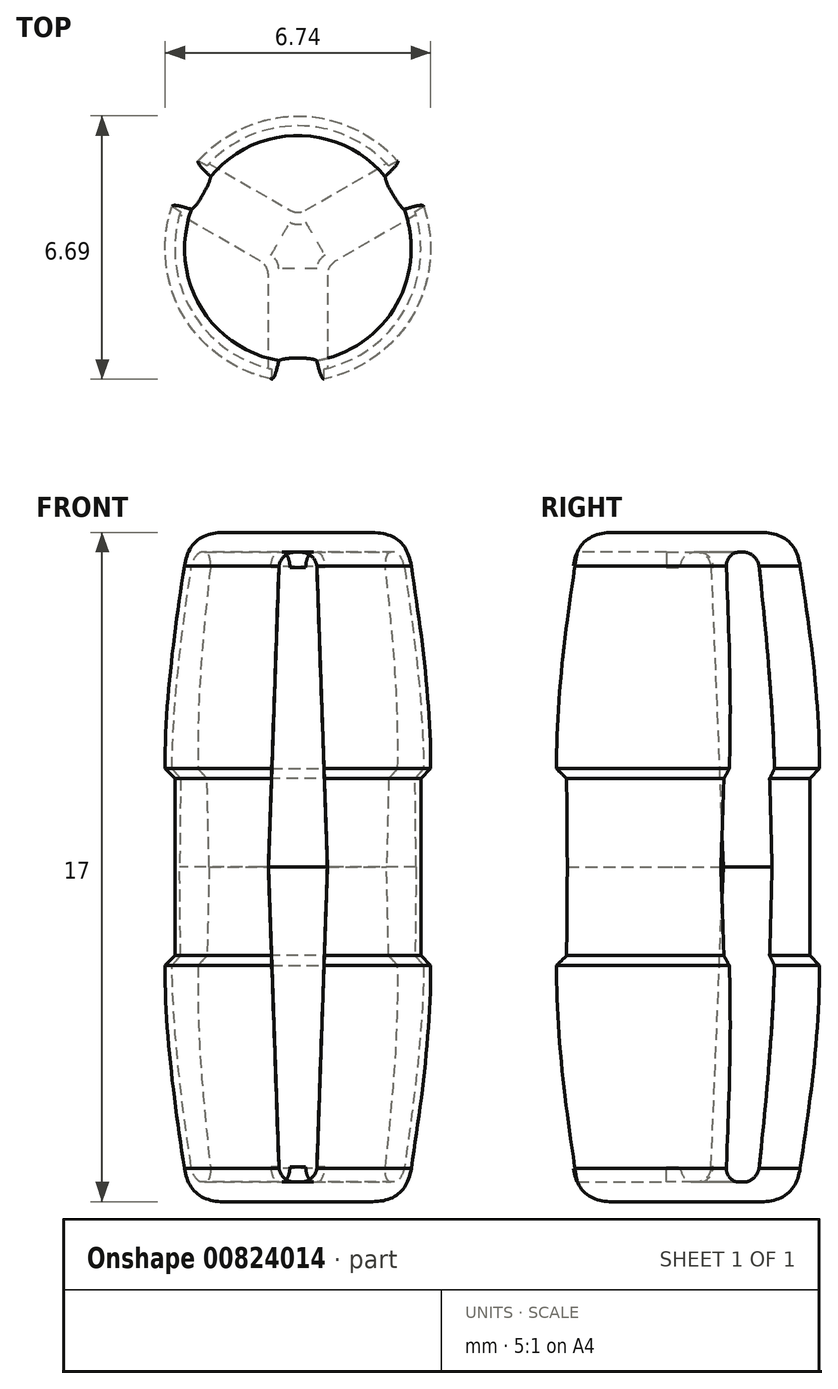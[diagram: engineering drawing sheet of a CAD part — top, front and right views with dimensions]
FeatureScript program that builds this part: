
annotation { "Feature Type Name" : "Feature", "Feature Type Description" : "" }
export const myFeature = defineFeature(function(context is Context, id is Id, definition is map)
    precondition{}
    {
        {
            var Q0;
            Q0=qCreatedBy(makeId("Top.planeOp"),FACE);
            var sketch = newSketch(context, id + "F0", { "sketchPlane" : qUnion([Q0])});
            skCircle(sketch, "E0", {"center": v(0, 0) * mm, "radius": 3.13 * mm});
            skSolve(sketch);
        }
        {
            var Q0;
            Q0 = qSketchRegion(id + "F0", true);
            extrude(context, id + "F1", {"entities" : qUnion([Q0]), "depth" : (4.5 / 2) * mm, "offsetDistance" : 25 * mm});
        }
        {
            var Q0;
            Q0=qCreatedBy(makeId("Front.planeOp"),FACE);
            var sketch = newSketch(context, id + "F2", { "sketchPlane" : qUnion([Q0])});
            skLineSegment(sketch, "E1", {"start": v(0, 0) * mm, "end": v(0, 2.29) * mm, "construction": true});
            skSolve(sketch);
        }
        {
            var Q0;
            Q0=makeQuery(id+"F1.opExtrude","CAP_FACE",FACE,{"disambiguationData":[OSD([sQuery(id+"F0.wireOp",EDGE,"E0")])],"isStart":false});
            extrude(context, id + "F3", {"entities" : qUnion([Q0]), "operationType" : NewBodyOperationType.ADD, "depth" : .25 * mm, "offsetDistance" : 25 * mm, "hasDraft" : true, "draftAngle" : 45 * degree});
        }
        {
            var Q0;
            Q0=makeQuery(id+"F3.opExtrude","CAP_FACE",FACE,{"disambiguationData":[OSD([sQuery(id+"F0.wireOp",EDGE,"E0")])],"isStart":false});
            cPlane(context, id + "F4", {"entities" : qUnion([Q0]), "cplaneType" : CPlaneType.OFFSET, "offset" : 6 * mm, "width" : 150 * mm, "height" : 150 * mm});
        }
        {
            var Q0;
            Q0=qCreatedBy(id+"F4.planeOp",FACE);
            var sketch = newSketch(context, id + "F5", { "sketchPlane" : qUnion([Q0])});
            skCircle(sketch, "E2", {"center": v(0, 0) * mm, "radius": 2.75 * mm});
            skSolve(sketch);
        }
        {
            var Q1;
            Q1=makeQuery(id+"F5.imprint","IMPRINT",FACE,{"disambiguationData":[TD([[makeQuery(id+"F5.imprint","IMPRINT",EDGE,{"derivedFrom":sQuery(id+"F5.wireOp",EDGE,"E2")}),1.0]])]});
            var Q2;
            Q2=makeQuery(id+"F3.opExtrude","CAP_FACE",FACE,{"disambiguationData":[OSD([sQuery(id+"F0.wireOp",EDGE,"E0")])],"isStart":false});
            loft(context, id + "F6", {"operationType" : NewBodyOperationType.ADD, "endCondition" : LoftEndDerivativeType.NORMAL_TO_PROFILE, "endMagnitude" : 1, "sheetProfilesArray" : [{ "sheetProfileEntities" : qUnion([Q1]) }, { "sheetProfileEntities" : qUnion([Q2]) }]});
        }
        {
            var Q0;
            Q0=makeQuery(id+"F6.opLoft","MID_CAP_EDGE",EDGE,{"disambiguationData":[OSD([sQuery(id+"F5.wireOp",EDGE,"E2")])],"capPos":0.0});
            fillet(context, id + "F7", {"entities" : qUnion([Q0]), "radius" : 1 * mm, "tangentPropagation" : true, "rho" : 0.5, "crossSection" : FilletCrossSection.CONIC, "allowEdgeOverflow" : false});
        }
        {
            var Q0;
            Q0=makeQuery(id+"F1.opExtrude","CAP_FACE",FACE,{"disambiguationData":[OSD([sQuery(id+"F0.wireOp",EDGE,"E0")])],"isStart":true});
            var sketch = newSketch(context, id + "F8", { "sketchPlane" : qUnion([Q0])});
            skLineSegment(sketch, "E3", {"start": v(-0.75, 5.66) * mm, "end": v(-0.75, 0.43) * mm});
            skLineSegment(sketch, "E4", {"start": v(-0.75, 0.43) * mm, "end": v(-5.28, -2.18) * mm});
            skLineSegment(sketch, "E5", {"start": v(-5.28, -2.18) * mm, "end": v(-4.53, -3.48) * mm});
            skLineSegment(sketch, "E6", {"start": v(-4.53, -3.48) * mm, "end": v(0, -0.87) * mm});
            skLineSegment(sketch, "E7", {"start": v(0, -0.87) * mm, "end": v(4.53, -3.48) * mm});
            skLineSegment(sketch, "E8", {"start": v(4.53, -3.48) * mm, "end": v(5.28, -2.18) * mm});
            skLineSegment(sketch, "E9", {"start": v(5.28, -2.18) * mm, "end": v(0.75, 0.43) * mm});
            skLineSegment(sketch, "E10", {"start": v(0.75, 0.43) * mm, "end": v(0.75, 5.66) * mm});
            skLineSegment(sketch, "E11", {"start": v(0.75, 5.66) * mm, "end": v(-0.75, 5.66) * mm});
            skLineSegment(sketch, "E12", {"start": v(0, 0) * mm, "end": v(0, 5.66) * mm, "construction": true});
            skLineSegment(sketch, "E13", {"start": v(0, 0) * mm, "end": v(-4.9, -2.83) * mm, "construction": true});
            skLineSegment(sketch, "E14", {"start": v(0, 0) * mm, "end": v(4.9, -2.83) * mm, "construction": true});
            skPoint(sketch, "E14.endSnap0", {"position": v(4.9, -2.83) * mm});
            skSolve(sketch);
        }
        {
            var Q0;
            Q0 = qSketchRegion(id + "F8", true);
            extrude(context, id + "F9", {"entities" : qUnion([Q0]), "operationType" : NewBodyOperationType.REMOVE, "oppositeDirection" : true, "depth" : 8 * mm, "offsetDistance" : 25 * mm, "hasDraft" : true, "draftAngle" : 2 * degree, "draftPullDirection" : true});
        }
        {
            var Q0;
            Q0=makeQuery(id+"F9.boolean.opBoolean","COPY",EDGE,{"derivedFrom":makeQuery(id+"F9.opExtrude","CAP_EDGE",EDGE,{"disambiguationData":[OSD([sQuery(id+"F8.wireOp",EDGE,"E6")])],"isStart":false})});
            var Q1;
            Q1=makeQuery(id+"F9.boolean.opBoolean","COPY",EDGE,{"derivedFrom":makeQuery(id+"F9.opExtrude","CAP_EDGE",EDGE,{"disambiguationData":[OSD([sQuery(id+"F8.wireOp",EDGE,"E4")])],"isStart":false})});
            var Q2;
            Q2=makeQuery(id+"F9.boolean.opBoolean","COPY",EDGE,{"derivedFrom":makeQuery(id+"F9.opExtrude","CAP_EDGE",EDGE,{"disambiguationData":[OSD([sQuery(id+"F8.wireOp",EDGE,"E3")])],"isStart":false})});
            var Q3;
            Q3=makeQuery(id+"F9.boolean.opBoolean","COPY",EDGE,{"derivedFrom":makeQuery(id+"F9.opExtrude","CAP_EDGE",EDGE,{"disambiguationData":[OSD([sQuery(id+"F8.wireOp",EDGE,"E10")])],"isStart":false})});
            var Q4;
            Q4=makeQuery(id+"F9.boolean.opBoolean","COPY",EDGE,{"derivedFrom":makeQuery(id+"F9.opExtrude","CAP_EDGE",EDGE,{"disambiguationData":[OSD([sQuery(id+"F8.wireOp",EDGE,"E7")])],"isStart":false})});
            var Q5;
            Q5=makeQuery(id+"F9.boolean.opBoolean","COPY",EDGE,{"derivedFrom":makeQuery(id+"F9.opExtrude","CAP_EDGE",EDGE,{"disambiguationData":[OSD([sQuery(id+"F8.wireOp",EDGE,"E9")])],"isStart":false})});
            var Q6;
            Q6=makeQuery(id+"F9.boolean.opBoolean","COPY",EDGE,{"derivedFrom":makeQuery(id+"F9.opExtrude","SWEPT_EDGE",EDGE,{"disambiguationData":[OSD([sQuery(id+"F8.wireOp",EDGE,"E9"),sQuery(id+"F8.wireOp",EDGE,"E10")])]})});
            var Q7;
            Q7=makeQuery(id+"F9.boolean.opBoolean","COPY",EDGE,{"derivedFrom":makeQuery(id+"F9.opExtrude","SWEPT_EDGE",EDGE,{"disambiguationData":[OSD([sQuery(id+"F8.wireOp",EDGE,"E6"),sQuery(id+"F8.wireOp",EDGE,"E7")])]})});
            var Q8;
            Q8=makeQuery(id+"F9.boolean.opBoolean","COPY",EDGE,{"derivedFrom":makeQuery(id+"F9.opExtrude","SWEPT_EDGE",EDGE,{"disambiguationData":[OSD([sQuery(id+"F8.wireOp",EDGE,"E3"),sQuery(id+"F8.wireOp",EDGE,"E4")])]})});
            fillet(context, id + "F10", {"entities" : qUnion([Q0, Q1, Q2, Q3, Q4, Q5, Q6, Q7, Q8]), "radius" : .4 * mm, "tangentPropagation" : true, "allowEdgeOverflow" : false});
        }
        {
            var Q0;
            Q0=makeQuery(id+"F1.opExtrude","SWEPT_BODY",BODY,{"disambiguationData":[OSD([sQuery(id+"F0.wireOp",EDGE,"E0")])]});
            var Q1;
            {var subQ0=sQuery(id+"F0.wireOp",EDGE,"E0");Q1=makeQuery(id+"F9.boolean.opBoolean","SPLIT",FACE,{"disambiguationData":[TD([makeQuery(id+"F9.opExtrude","SWEPT_FACE",FACE,{"disambiguationData":[OSD([sQuery(id+"F8.wireOp",EDGE,"E3")])]})])],"derivedFrom":makeQuery(id+"F1.opExtrude","CAP_FACE",FACE,{"disambiguationData":[OSD([subQ0])],"isStart":true})});}
            mirror(context, id + "F11", {"operationType" : NewBodyOperationType.ADD, "entities" : qUnion([Q0]), "mirrorPlane" : qUnion([Q1])});
        }
    });
